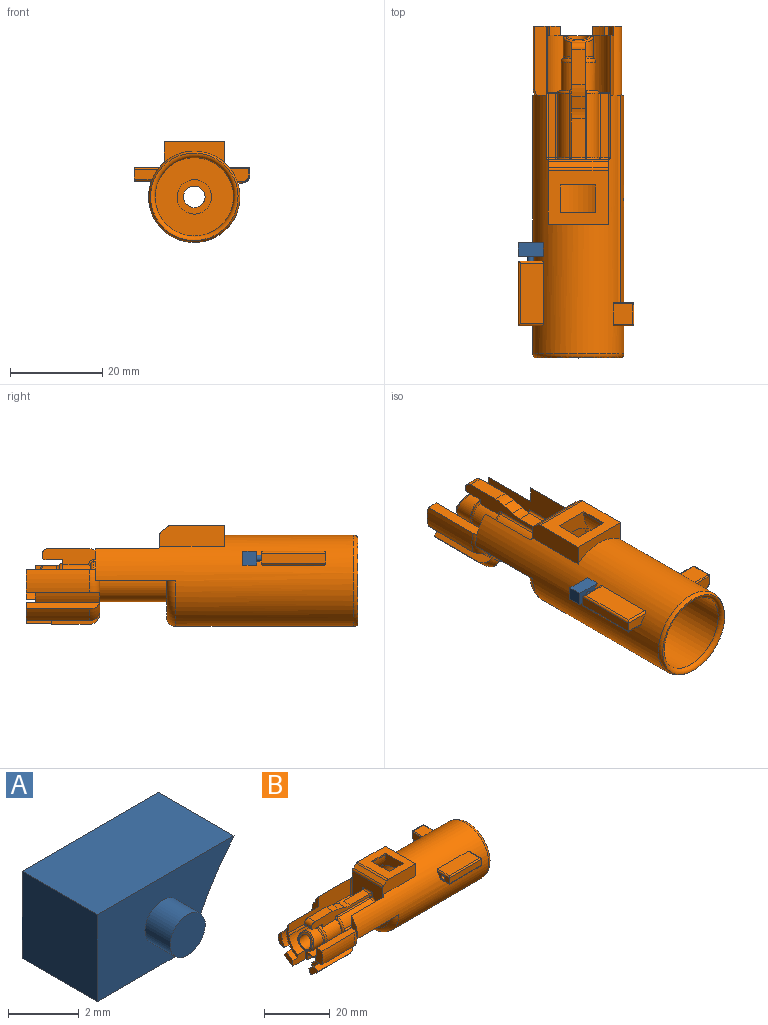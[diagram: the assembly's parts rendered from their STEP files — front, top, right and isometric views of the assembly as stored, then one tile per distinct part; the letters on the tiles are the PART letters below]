
ASSEMBLY  parts=2 mates=1
PART A: 8 faces, bbox 5.4x4x3 mm
  f0: plane 5.45x3mm, normal (0,0,1), area 16.3mm2, adj f1,f3,f4,f5
  f1: plane 3x3mm, normal (-1,0,0), area 9mm2, adj f0,f2,f4,f5
  f2: plane 3.7x3mm, normal (0,0,-1), area 11.1mm2, adj f1,f3,f4,f5
  f3: cylinder r=9.9mm len=3mm, axis (0,1,0), area 10.5mm2, adj f0,f2,f4,f5
  f4: plane 5.45x3mm, normal (0,-1,0), area 11.8mm2, adj f0,f1,f2,f3,f6
  f5: plane 5.45x3mm, normal (0,1,0), area 13.4mm2, adj f0,f1,f2,f3
  f6: cylinder r=0.7mm len=1.4mm, axis (0,1,0), area 4.4mm2, adj f4,f7
  f7: plane 1.4x1.4mm, normal (0,-1,0), area 1.5mm2, adj f6
PART B: 160 faces, bbox 72.7x25.5x23 mm
  f0: cylinder r=0.75mm len=1.5mm, axis (-1,0,0), area 4.7mm2, adj f41,f156
  f1: cylinder r=7.75mm len=13.98mm, axis (1,0,0), area 27mm2, adj f11,f61,f74,f78,f80,f158
  f2: plane 17.5x5.4mm, normal (0,0,-1), area 80.3mm2, adj f17,f43,f98,f99,f108,f158,f159
  f3: plane 17.5x5.4mm, normal (0,0,-1), area 80.5mm2, adj f17,f43,f68,f98,f99,f109,f157,f159
  f4: cylinder r=1.35mm len=45mm, axis (-1,0,0), area 90.8mm2, adj f17,f36,f109
  f5: cylinder r=4.5mm len=13.9mm, axis (-1,0,0), area 59.9mm2, adj f101,f105,f106,f131,f135,f144
  f6: plane 13x8.9mm, normal (-1,0,0), area 81.6mm2, adj f21,f22,f52,f140,f142,f144,f146,f147
  f7: plane 26.5x7mm, normal (0,-1,0), area 123.8mm2, adj f17,f73,f75,f83,f103,f107,f109,f138
  f8: cylinder r=4.5mm len=13.9mm, axis (-1,0,0), area 59.9mm2, adj f103,f105,f107,f130,f132,f150
  f9: plane 7.79x7.24mm, normal (-1,0,0), area 2.9mm2, adj f15,f105,f134,f137
  f10: plane 3.95x3.8mm, normal (-1,0,0), area 7.7mm2, adj f63,f64,f66,f79
  f11: plane 6.58x4.34mm, normal (-1,0,0), area 6.1mm2, adj f1,f14,f54,f60,f72,f80,f81,f82
  f12: cylinder r=2.35mm len=12.92mm, axis (-1,0,0), area 186.2mm2, adj f30,f76,f77,f89,f90
  f13: cylinder r=3.25mm len=6.5mm, axis (1,0,0), area 78mm2, adj f94,f95,f96,f97,f155
  f14: plane 16.31x3mm, normal (0,0,-1), area 33.4mm2, adj f11,f54,f55,f57,f72,f158
  f15: cylinder r=3.75mm len=7.5mm, axis (1,0,0), area 125.8mm2, adj f9,f44,f45,f47,f51,f133,f134,f136
  f16: plane 8.33x3mm, normal (0,0,1), area 25mm2, adj f44,f45,f85,f147
  f17: cylinder r=9.9mm len=56.04mm, axis (-1,0,0), area 2370.3mm2, adj f2,f3,f4,f7,f21,f22,f24,f31
  f18: cylinder r=8.5mm len=40mm, axis (-1,0,0), area 2053.1mm2, adj f23,f25,f27,f88,f91,f128,f129
  f19: plane 6x0.48mm, normal (0,-1,0), area 2.9mm2, adj f23,f25,f26,f128
  f20: plane 6x0.48mm, normal (0,1,0), area 2.9mm2, adj f23,f25,f26,f129
  f21: plane 14x4.53mm, normal (0,1,0), area 61.8mm2, adj f6,f17,f24,f26,f28,f52,f53
  f22: plane 14x4.53mm, normal (0,-1,0), area 61.8mm2, adj f6,f17,f24,f26,f28,f52,f53
  f23: plane 12.15x6.05mm, normal (-1,0,0), area 32.5mm2, adj f18,f19,f20,f26,f128,f129
  f24: plane 13x4.53mm, normal (1,0,0), area 37.3mm2, adj f17,f21,f22,f26
  f25: plane 12.15x6.05mm, normal (1,0,0), area 32.5mm2, adj f18,f19,f20,f26,f128,f129
  f26: plane 13x11.63mm, normal (0,0,1), area 105.6mm2, adj f19,f20,f21,f22,f23,f24,f25,f53
  f27: plane 17x17mm, normal (1,0,0), area 182.8mm2, adj f18,f29
  f28: plane 13x1.37mm, normal (-0.62,0,0.78), area 22.8mm2, adj f21,f22,f52,f53
  f29: cylinder r=3.75mm len=16mm, axis (-1,0,0), area 377mm2, adj f27,f30
  f30: plane 7.5x7.5mm, normal (1,0,0), area 26.8mm2, adj f12,f29
  f31: plane 4.47x1.07mm, normal (0,0,-1), area 4.8mm2, adj f17,f32,f117,f127
  f32: cylinder r=1.5mm len=4.47mm, axis (-1,0,0), area 10.5mm2, adj f31,f33,f118,f126
  f33: plane 4.47x1.63mm, normal (0,1,0), area 7.3mm2, adj f32,f119,f122,f125
  f34: plane 4.47x4.19mm, normal (0,0,1), area 18.7mm2, adj f17,f120,f122,f123
  f35: plane 3.97x2.87mm, normal (1,0,0), area 8.5mm2, adj f17,f117,f118,f119,f120
  f36: plane 3.97x2.87mm, normal (-1,0,0), area 9mm2, adj f4,f17,f123,f125,f126,f127
  f37: plane 13.13x5.01mm, normal (0,0,1), area 65.8mm2, adj f17,f111,f112,f113
  f38: plane 14x2.13mm, normal (0,-1,0), area 29.8mm2, adj f40,f41,f113,f116
  f39: plane 13.13x3.27mm, normal (0,0,-1), area 42.9mm2, adj f17,f114,f115,f116
  f40: plane 5.1x2.13mm, normal (1,0,0), area 9.4mm2, adj f17,f38,f111,f114
  f41: plane 5.1x2.13mm, normal (-1,0,0), area 7.7mm2, adj f0,f17,f38,f112,f115
  f42: plane 28.5x7mm, normal (0,1,0), area 118.1mm2, adj f17,f56,f57,f82,f101,f106,f108,f139
  f43: cylinder r=4.5mm len=14.5mm, axis (-1,0,0), area 205mm2, adj f2,f3,f98,f99
  f44: plane 25x3.63mm, normal (0,1,0), area 50.3mm2, adj f15,f16,f46,f47,f48,f49,f50,f84
  f45: plane 25x3.63mm, normal (0,-1,0), area 50.3mm2, adj f15,f16,f46,f47,f48,f49,f50,f84
  f46: plane 3x2.61mm, normal (0.29,0,0.96), area 8.2mm2, adj f44,f45,f84,f85
  f47: plane 3x1.13mm, normal (-1,0,0), area 2.8mm2, adj f15,f44,f45,f48
  f48: plane 3.9x3mm, normal (0,0,-1), area 11.7mm2, adj f44,f45,f47,f86
  f49: plane 7.68x3mm, normal (0,0,1), area 23mm2, adj f44,f45,f84,f87
  f50: plane 3x0.4mm, normal (-1,0,0), area 1.2mm2, adj f44,f45,f86,f87
  f51: torus R=2.75mm, axis (-1,0,0), area 18.3mm2, adj f15,f155
  f52: cylinder r=1mm len=13mm, axis (0,-1,0), area 11.6mm2, adj f6,f21,f22,f28
  f53: cylinder r=1mm len=13mm, axis (0,-1,0), area 8.8mm2, adj f21,f22,f26,f28
  f54: plane 2x1.93mm, normal (0,1,0), area 3.9mm2, adj f11,f14,f57,f82
  f55: cylinder r=9.75mm len=13.7mm, axis (1,0,0), area 69.3mm2, adj f14,f56,f57,f158
  f56: plane 15.06x2.48mm, normal (0,0,1), area 36.2mm2, adj f42,f55,f57,f108,f158
  f57: plane 5x3mm, normal (-1,0,0), area 13.8mm2, adj f14,f42,f54,f55,f56,f82
  f58: cylinder r=9.75mm len=13.7mm, axis (1,0,0), area 55.7mm2, adj f59,f61,f62,f158
  f59: plane 16.08x1.56mm, normal (0,-0.68,0.73), area 31mm2, adj f58,f60,f62,f72,f158
  f60: cylinder r=7.75mm len=2.31mm, axis (1,0,0), area 6.2mm2, adj f11,f59,f61,f62
  f61: plane 16.16x2.09mm, normal (0,0.94,-0.33), area 31.3mm2, adj f1,f58,f60,f62,f158
  f62: plane 3.94x3.78mm, normal (-1,0,0), area 7.2mm2, adj f58,f59,f60,f61
  f63: plane 16.18x1.86mm, normal (0,0.82,0.57), area 31.4mm2, adj f10,f64,f66,f71,f157
  f64: cylinder r=9.75mm len=13.7mm, axis (1,0,0), area 66.1mm2, adj f10,f63,f65,f78,f79,f157
  f65: plane 10.66x2.2mm, normal (0,-0.99,-0.1), area 20.1mm2, adj f64,f70,f78,f157
  f66: cylinder r=7.75mm len=2.63mm, axis (1,0,0), area 6.4mm2, adj f10,f63,f75,f79
  f67: cylinder r=7.75mm len=4.84mm, axis (1,0,0), area 10.1mm2, adj f68,f69,f75
  f68: cylinder r=2.5mm len=15.98mm, axis (1,0,0), area 111.4mm2, adj f3,f67,f69,f71,f73,f109,f157
  f69: plane 4.86x2.84mm, normal (-1,0,0), area 7.2mm2, adj f67,f68
  f70: cylinder r=7.75mm len=10.48mm, axis (1,0,0), area 5.2mm2, adj f65,f74,f78,f157
  f71: cylinder r=7.75mm len=13.98mm, axis (1,0,0), area 21.2mm2, adj f63,f68,f75,f157
  f72: cylinder r=7.75mm len=13.98mm, axis (1,0,0), area 35.1mm2, adj f11,f14,f59,f158
  f73: cylinder r=7.75mm len=13mm, axis (1,0,0), area 35.5mm2, adj f7,f68,f75,f109
  f74: cylinder r=3.63mm len=10.5mm, axis (1,0,0), area 38.3mm2, adj f1,f70,f78,f99,f157,f158
  f75: plane 10.47x4.75mm, normal (-1,0,0), area 9.9mm2, adj f7,f66,f67,f71,f73,f79,f81,f83
  f76: plane 5.58x2.27mm, normal (-1,0,0), area 3.5mm2, adj f12,f89,f90,f96
  f77: plane 5.65x2.46mm, normal (-0.93,0,0.37), area 4.7mm2, adj f12,f89,f90,f95
  f78: plane 6x3.39mm, normal (-1,0,0), area 6.1mm2, adj f1,f64,f65,f70,f74,f79,f80,f81
  f79: plane 5.5x3.23mm, normal (0,-1,0), area 15.6mm2, adj f10,f64,f66,f75,f78,f81
  f80: plane 3.5x1.1mm, normal (0,1,0), area 3.8mm2, adj f1,f11,f78,f81
  f81: cylinder r=6.75mm len=13.4mm, axis (1,0,0), area 222.4mm2, adj f11,f75,f78,f79,f80,f82,f83,f100
  f82: cylinder r=2mm len=14.5mm, axis (1,0,0), area 12.4mm2, adj f11,f42,f54,f57,f81,f100
  f83: cylinder r=2mm len=12.5mm, axis (1,0,0), area 11.2mm2, adj f7,f75,f81,f100
  f84: cylinder r=9mm len=3mm, axis (0,-1,0), area 7.9mm2, adj f44,f45,f46,f49
  f85: cylinder r=8mm len=3mm, axis (0,1,0), area 7mm2, adj f16,f44,f45,f46
  f86: cylinder r=0.6mm len=3mm, axis (0,1,0), area 2.8mm2, adj f44,f45,f48,f50
  f87: cylinder r=1.5mm len=3mm, axis (0,-1,0), area 7.1mm2, adj f44,f45,f49,f50
  f88: torus R=9.5mm, axis (1,0,0), area 87.5mm2, adj f18,f110
  f89: cylinder r=3mm len=1.12mm, axis (0,1,0), area 0.6mm2, adj f12,f76,f77,f97
  f90: cylinder r=3mm len=1.12mm, axis (0,1,0), area 0.6mm2, adj f12,f76,f77,f94
  f91: cylinder r=0.8mm len=1.6mm, axis (0,-1,0), area 2.7mm2, adj f18,f93
  f92: cylinder r=1.25mm len=2.5mm, axis (0,-1,0), area 6.4mm2, adj f17,f93
  f93: plane 2.5x2.5mm, normal (0,1,0), area 2.9mm2, adj f91,f92
  f94: bspline ~2.04x0.64mm, area 0.7mm2, adj f13,f90,f95,f96
  f95: bspline ~6.44x2.8mm, area 4.8mm2, adj f13,f77,f94,f97
  f96: torus R=2.85mm, axis (-1,0,0), area 5.3mm2, adj f13,f76,f94,f97
  f97: bspline ~2.47x0.85mm, area 0.7mm2, adj f13,f89,f95,f96
  f98: plane 15.8x7.9mm, normal (-1,0,0), area 66.2mm2, adj f2,f3,f43,f159
  f99: plane 14.9x7.34mm, normal (1,0,0), area 54.8mm2, adj f2,f3,f43,f74,f157,f158
  f100: plane 14x6.75mm, normal (-1,0,0), area 40mm2, adj f81,f82,f83,f105,f106,f107
  f101: plane 2.59x0.5mm, normal (-1,0,0), area 0.1mm2, adj f5,f42,f102,f106,f131,f139
  f102: plane 13.89x1.6mm, normal (0,0,1), area 22.2mm2, adj f101,f131,f139,f142
  f103: plane 2.59x0.5mm, normal (-1,0,0), area 0.1mm2, adj f7,f8,f104,f107,f130,f138
  f104: plane 13.89x1.6mm, normal (0,0,1), area 22.2mm2, adj f103,f130,f138,f153
  f105: torus R=3.9mm, axis (1,0,0), area 20.1mm2, adj f5,f8,f9,f100,f106,f107,f133,f136
  f106: cylinder r=1.21mm len=2.53mm, axis (0,-1,0), area 1.3mm2, adj f5,f42,f100,f101,f105
  f107: cylinder r=1.21mm len=2.53mm, axis (0,1,0), area 1.3mm2, adj f7,f8,f100,f103,f105
  f108: plane 7x2.9mm, normal (-1,0,0), area 8.4mm2, adj f2,f17,f42,f56,f158
  f109: plane 7x2.9mm, normal (-1,0,0), area 11.4mm2, adj f3,f4,f7,f17,f68,f73
  f110: torus R=8.55mm, axis (1,0,0), area 65.5mm2, adj f17,f88
  f111: cylinder r=0.43mm len=5.45mm, axis (0,1,0), area 3.5mm2, adj f17,f37,f40,f113
  f112: cylinder r=0.43mm len=5.45mm, axis (0,-1,0), area 3.5mm2, adj f17,f37,f41,f113
  f113: cylinder r=0.43mm len=14mm, axis (1,0,0), area 9.3mm2, adj f37,f38,f111,f112
  f114: cylinder r=0.43mm len=3.87mm, axis (0,-1,0), area 2.4mm2, adj f17,f39,f40,f116
  f115: cylinder r=0.43mm len=3.87mm, axis (0,1,0), area 2.4mm2, adj f17,f39,f41,f116
  f116: cylinder r=0.43mm len=14mm, axis (-1,0,0), area 9.3mm2, adj f38,f39,f114,f115
  f117: cylinder r=0.27mm len=1.16mm, axis (0,-1,0), area 0.5mm2, adj f17,f31,f35,f118
  f118: torus R=1.23mm, axis (1,0,0), area 0.9mm2, adj f32,f35,f117,f119
  f119: cylinder r=0.27mm len=1.63mm, axis (0,0,-1), area 0.7mm2, adj f33,f35,f118,f121
  f120: cylinder r=0.27mm len=4.19mm, axis (0,1,0), area 1.7mm2, adj f17,f34,f35,f121
  f121: sphere r=0.27mm, area 0.1mm2, adj f119,f120,f122
  f122: cylinder r=0.27mm len=4.47mm, axis (-1,0,0), area 1.9mm2, adj f33,f34,f121,f124
  f123: cylinder r=0.27mm len=4.19mm, axis (0,-1,0), area 1.7mm2, adj f17,f34,f36,f124
  f124: sphere r=0.27mm, area 0.2mm2, adj f122,f123,f125
  f125: cylinder r=0.27mm len=1.63mm, axis (0,0,1), area 0.7mm2, adj f33,f36,f124,f126
  f126: torus R=1.23mm, axis (1,0,0), area 0.9mm2, adj f32,f36,f125,f127
  f127: cylinder r=0.27mm len=1.16mm, axis (0,1,0), area 0.5mm2, adj f17,f31,f36,f126
  f128: cylinder r=7.97mm len=6mm, axis (-1,0,0), area 37.1mm2, adj f18,f19,f23,f25
  f129: cylinder r=7.97mm len=6mm, axis (-1,0,0), area 37.1mm2, adj f18,f20,f23,f25
  f130: cylinder r=0.5mm len=13.89mm, axis (-1,0,0), area 9.5mm2, adj f8,f103,f104,f151
  f131: cylinder r=0.5mm len=13.89mm, axis (-1,0,0), area 9.5mm2, adj f5,f101,f102,f143
  f132: cylinder r=0.5mm len=13.9mm, axis (-1,0,0), area 8.1mm2, adj f8,f44,f133,f149
  f133: bspline ~1.33x1.16mm, area 0.9mm2, adj f15,f44,f105,f132,f134
  f134: cylinder r=0.5mm len=0.3mm, axis (0,0,-1), area 0mm2, adj f9,f15,f133
  f135: cylinder r=0.5mm len=13.9mm, axis (-1,0,0), area 8.1mm2, adj f5,f45,f136,f145
  f136: bspline ~1.61x1.33mm, area 0.9mm2, adj f15,f45,f105,f135,f137
  f137: cylinder r=0.5mm len=0.3mm, axis (0,0,1), area 0mm2, adj f9,f15,f136
  f138: cylinder r=0.5mm len=13.89mm, axis (1,0,0), area 10.9mm2, adj f7,f103,f104,f154
  f139: cylinder r=0.5mm len=13.89mm, axis (-1,0,0), area 10.9mm2, adj f42,f101,f102,f141
  f140: cylinder r=0.5mm len=6.47mm, axis (0,0,-1), area 4.9mm2, adj f6,f17,f42,f141
  f141: sphere r=0.5mm, area 0.2mm2, adj f139,f140,f142
  f142: cylinder r=0.5mm len=1.6mm, axis (0,-1,0), area 1.3mm2, adj f6,f102,f141,f143
  f143: sphere r=0.5mm, area 0.3mm2, adj f131,f142,f144
  f144: torus R=5mm, axis (1,0,0), area 3.5mm2, adj f5,f6,f143,f145
  f145: sphere r=0.5mm, area 0.3mm2, adj f135,f144,f146
  f146: cylinder r=0.5mm len=1.49mm, axis (0,0,1), area 1mm2, adj f6,f45,f145,f147
  f147: cylinder r=0.5mm len=4mm, axis (0,1,0), area 2.7mm2, adj f6,f16,f146,f148
  f148: cylinder r=0.5mm len=1.49mm, axis (0,0,-1), area 1mm2, adj f6,f44,f147,f149
  f149: sphere r=0.5mm, area 0.3mm2, adj f132,f148,f150
  f150: torus R=5mm, axis (1,0,0), area 3.5mm2, adj f6,f8,f149,f151
  f151: sphere r=0.5mm, area 0.3mm2, adj f130,f150,f153
  f152: cylinder r=0.5mm len=6.47mm, axis (0,0,1), area 4.9mm2, adj f6,f7,f17,f154
  f153: cylinder r=0.5mm len=1.6mm, axis (0,-1,0), area 1.3mm2, adj f6,f104,f151,f154
  f154: sphere r=0.5mm, area 0.4mm2, adj f138,f152,f153
  f155: torus R=3.9mm, axis (-1,0,0), area 10.8mm2, adj f13,f51
  f156: plane 1.5x1.5mm, normal (-1,0,0), area 1.8mm2, adj f0
  f157: torus R=7.45mm, axis (1,0,0), area 27.1mm2, adj f3,f63,f64,f65,f68,f70,f71,f74
  f158: torus R=7.45mm, axis (1,0,0), area 27.6mm2, adj f1,f2,f14,f55,f56,f58,f59,f61
  f159: torus R=7.9mm, axis (1,0,0), area 90.5mm2, adj f2,f3,f17,f98
PLACE A t=(-8.14,-20.51,3.38)mm
PLACE B rot(axis=(0,0,-1),90deg) t=(4.86,-2.51,-0.02)mm
MATE fastened B.f0 <-> A.f6  axis (0,1,0) through (-5.54,-24.51,4.88)mm
